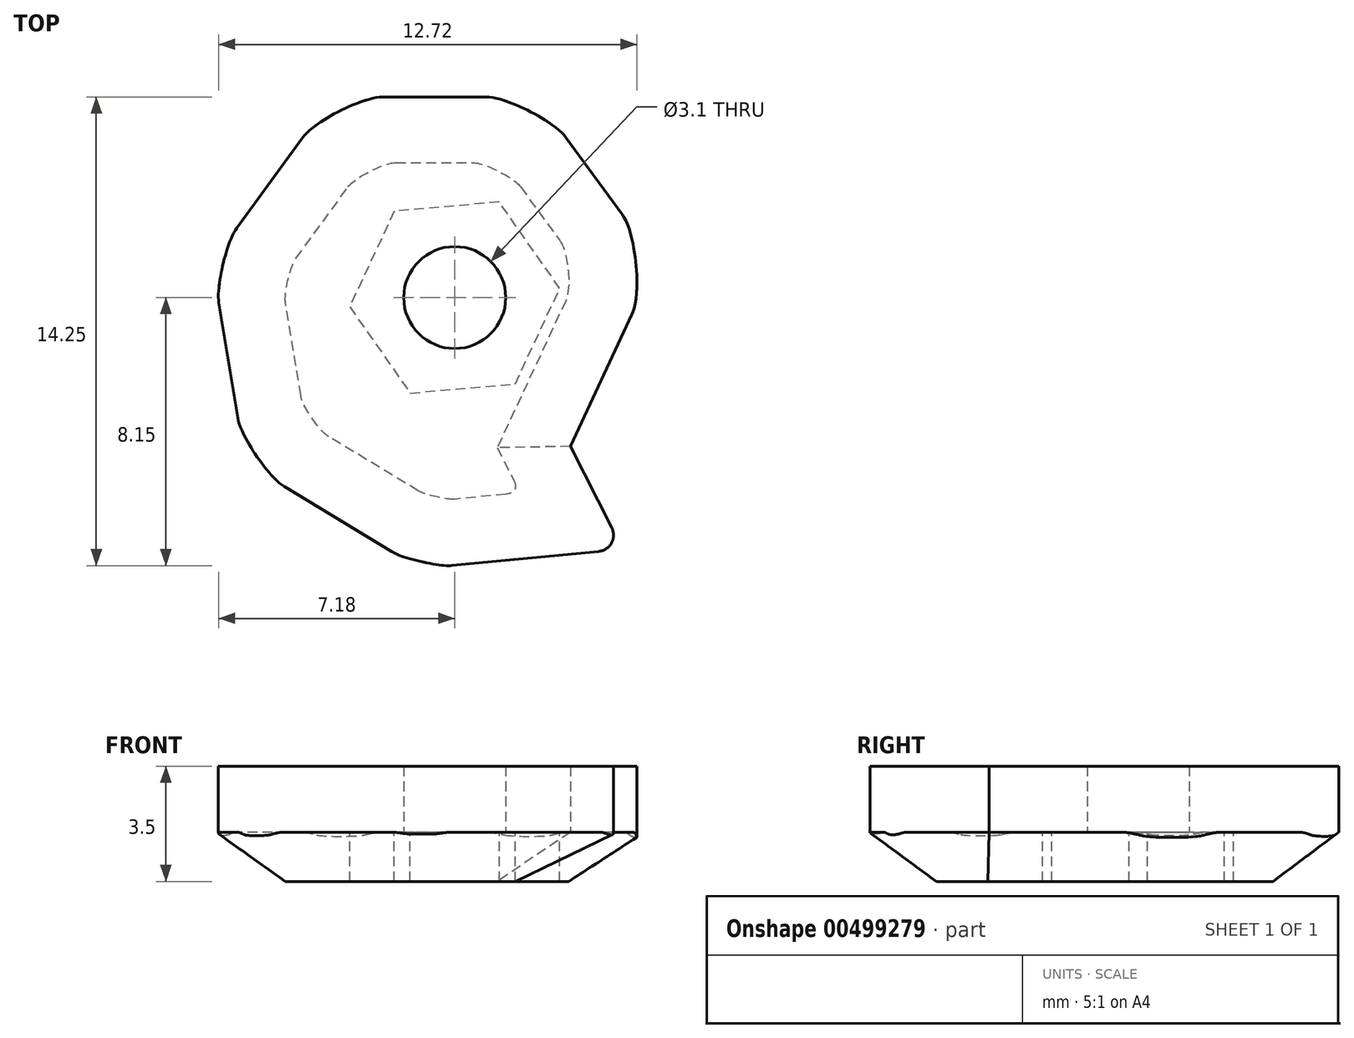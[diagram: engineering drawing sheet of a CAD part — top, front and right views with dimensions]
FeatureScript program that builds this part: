
annotation { "Feature Type Name" : "Feature", "Feature Type Description" : "" }
export const myFeature = defineFeature(function(context is Context, id is Id, definition is map)
    precondition{}
    {
        {
            var Q0;
            Q0=qCreatedBy(makeId("Top.planeOp"),FACE);
            var sketch = newSketch(context, id + "F0", { "sketchPlane" : qUnion([Q0])});
            skCircle(sketch, "E0", {"center": v(0, 0) * mm, "radius": 1.55 * mm});
            skLineSegment(sketch, "E1", {"start": v(0, 0) * mm, "end": v(4.62, -2.15) * mm, "construction": true});
            skLineSegment(sketch, "E2", {"start": v(0, 0) * mm, "end": v(4.52, 3.3) * mm, "construction": true});
            skLineSegment(sketch, "E3", {"start": v(0, 0) * mm, "end": v(0, 6.1) * mm, "construction": true});
            skLineSegment(sketch, "E4", {"start": v(0, 0) * mm, "end": v(-7, -1.15) * mm, "construction": true});
            skLineSegment(sketch, "E5", {"start": v(3.52, -4.53) * mm, "end": v(6.14, 1.1) * mm});
            skLineSegment(sketch, "E6", {"start": v(6.14, 1.1) * mm, "end": v(2.48, 6.1) * mm});
            skLineSegment(sketch, "E7", {"start": v(2.48, 6.1) * mm, "end": v(-3.72, 6.1) * mm});
            skLineSegment(sketch, "E8", {"start": v(-7.37, 1.1) * mm, "end": v(-6.37, -5.03) * mm});
            skLineSegment(sketch, "E9", {"start": v(0, 0) * mm, "end": v(-5.33, 3.9) * mm, "construction": true});
            skLineSegment(sketch, "E10", {"start": v(-3.72, 6.1) * mm, "end": v(-7.37, 1.1) * mm});
            skLineSegment(sketch, "E11", {"start": v(0, 0) * mm, "end": v(-3.94, -6.5) * mm, "construction": true});
            skLineSegment(sketch, "E12", {"start": v(-6.37, -5.03) * mm, "end": v(-1.07, -8.24) * mm});
            skLineSegment(sketch, "E13", {"start": v(0, 0) * mm, "end": v(0.77, -8.06) * mm, "construction": true});
            skLineSegment(sketch, "E14", {"start": v(-1.07, -8.24) * mm, "end": v(5.1, -7.65) * mm});
            skLineSegment(sketch, "E15", {"start": v(5.1, -7.65) * mm, "end": v(3.52, -4.53) * mm});
            skSolve(sketch);
        }
        {
            var Q0;
            Q0=makeQuery(id+"F0.imprint","IMPRINT",FACE,{"disambiguationData":[TD([[makeQuery(id+"F0.imprint","IMPRINT",EDGE,{"derivedFrom":sQuery(id+"F0.wireOp",EDGE,"E0")}),-1.0]])]});
            extrude(context, id + "F1", {"entities" : qUnion([Q0]), "depth" : 2 * mm});
        }
        {
            var Q0;
            Q0=makeQuery(id+"F1.opExtrude","CAP_FACE",FACE,{"disambiguationData":[OSD([sQuery(id+"F0.wireOp",EDGE,"E0"),sQuery(id+"F0.wireOp",EDGE,"E5"),sQuery(id+"F0.wireOp",EDGE,"E6"),sQuery(id+"F0.wireOp",EDGE,"E7"),sQuery(id+"F0.wireOp",EDGE,"E8"),sQuery(id+"F0.wireOp",EDGE,"E10"),sQuery(id+"F0.wireOp",EDGE,"E12"),sQuery(id+"F0.wireOp",EDGE,"E14"),sQuery(id+"F0.wireOp",EDGE,"E15")])],"isStart":true});
            var sketch = newSketch(context, id + "F2", { "sketchPlane" : qUnion([Q0])});
            skCircle(sketch, "E16.cCircle", {"center": v(0, 0) * mm, "radius": 2.77 * mm, "construction": true});
            skLineSegment(sketch, "E16.0", {"start": v(3.2, -0.28) * mm, "end": v(1.35, -2.9) * mm});
            skLineSegment(sketch, "E16.1", {"start": v(1.35, -2.9) * mm, "end": v(-1.84, -2.62) * mm});
            skLineSegment(sketch, "E16.2", {"start": v(-1.84, -2.62) * mm, "end": v(-3.2, 0.28) * mm});
            skLineSegment(sketch, "E16.3", {"start": v(-3.2, 0.28) * mm, "end": v(-1.35, 2.9) * mm});
            skLineSegment(sketch, "E16.4", {"start": v(-1.35, 2.9) * mm, "end": v(1.84, 2.62) * mm});
            skLineSegment(sketch, "E16.5", {"start": v(1.84, 2.62) * mm, "end": v(3.2, -0.28) * mm});
            skPoint(sketch, "E16.0.midPoint", {"position": v(2.27, -1.6) * mm});
            skSolve(sketch);
        }
        {
            var Q0;
            Q0=makeQuery(id+"F2.imprint","IMPRINT",FACE,{"disambiguationData":[TD([[makeQuery(id+"F2.imprint","IMPRINT",EDGE,{"derivedFrom":sQuery(id+"F2.wireOp",EDGE,"E16.0")}),1.0]])]});
            extrude(context, id + "F3", {"entities" : qUnion([Q0]), "operationType" : NewBodyOperationType.ADD, "depth" : 1.5 * mm});
        }
        {
            var Q0;
            Q0=makeQuery(id+"F3.opExtrude","CAP_EDGE",EDGE,{"disambiguationData":[OSD([sQuery(id+"F0.wireOp",EDGE,"E5")])],"isStart":false});
            var Q1;
            Q1=makeQuery(id+"F3.opExtrude","CAP_EDGE",EDGE,{"disambiguationData":[OSD([sQuery(id+"F0.wireOp",EDGE,"E15")])],"isStart":false});
            var Q2;
            Q2=makeQuery(id+"F3.opExtrude","CAP_EDGE",EDGE,{"disambiguationData":[OSD([sQuery(id+"F0.wireOp",EDGE,"E14")])],"isStart":false});
            var Q3;
            Q3=makeQuery(id+"F3.opExtrude","CAP_EDGE",EDGE,{"disambiguationData":[OSD([sQuery(id+"F0.wireOp",EDGE,"E12")])],"isStart":false});
            var Q4;
            Q4=makeQuery(id+"F3.opExtrude","CAP_EDGE",EDGE,{"disambiguationData":[OSD([sQuery(id+"F0.wireOp",EDGE,"E8")])],"isStart":false});
            var Q5;
            Q5=makeQuery(id+"F3.opExtrude","CAP_EDGE",EDGE,{"disambiguationData":[OSD([sQuery(id+"F0.wireOp",EDGE,"E10")])],"isStart":false});
            var Q6;
            Q6=makeQuery(id+"F3.opExtrude","CAP_EDGE",EDGE,{"disambiguationData":[OSD([sQuery(id+"F0.wireOp",EDGE,"E7")])],"isStart":false});
            var Q7;
            Q7=makeQuery(id+"F3.opExtrude","CAP_EDGE",EDGE,{"disambiguationData":[OSD([sQuery(id+"F0.wireOp",EDGE,"E6")])],"isStart":false});
            chamfer(context, id + "F4", {"entities" : qUnion([Q0, Q1, Q2, Q3, Q4, Q5, Q6, Q7]), "chamferType" : ChamferType.TWO_OFFSETS, "width1" : 1.5 * mm, "oppositeDirection" : false, "width2" : 2 * mm, "tangentPropagation" : true});
        }
        {
            var Q0;
            {var subQ0=sQuery(id+"F0.wireOp",EDGE,"E12");var subQ1=sQuery(id+"F0.wireOp",EDGE,"E8");Q0=makeQuery(id+"F3.boolean.opBoolean","MERGE",EDGE,{"derivedFrom":[makeQuery(id+"F1.opExtrude","SWEPT_EDGE",EDGE,{"disambiguationData":[OSD([subQ1,subQ0])]}),makeQuery(id+"F3.opExtrude","SWEPT_EDGE",EDGE,{"disambiguationData":[OSD([subQ1,subQ0])]})]});}
            var Q1;
            Q1=makeQuery(id+"F4.opChamfer","BLEND_EDGE",EDGE,{"blendedFrom":[makeQuery(id+"F3.opExtrude","CAP_EDGE",EDGE,{"disambiguationData":[OSD([sQuery(id+"F0.wireOp",EDGE,"E8")])],"isStart":false}),makeQuery(id+"F3.opExtrude","CAP_EDGE",EDGE,{"disambiguationData":[OSD([sQuery(id+"F0.wireOp",EDGE,"E12")])],"isStart":false})],"blendedInto":[]});
            var Q2;
            {var subQ0=sQuery(id+"F0.wireOp",EDGE,"E10");var subQ1=sQuery(id+"F0.wireOp",EDGE,"E8");Q2=makeQuery(id+"F3.boolean.opBoolean","MERGE",EDGE,{"derivedFrom":[makeQuery(id+"F1.opExtrude","SWEPT_EDGE",EDGE,{"disambiguationData":[OSD([subQ1,subQ0])]}),makeQuery(id+"F3.opExtrude","SWEPT_EDGE",EDGE,{"disambiguationData":[OSD([subQ1,subQ0])]})]});}
            var Q3;
            Q3=makeQuery(id+"F4.opChamfer","BLEND_EDGE",EDGE,{"blendedFrom":[makeQuery(id+"F3.opExtrude","CAP_EDGE",EDGE,{"disambiguationData":[OSD([sQuery(id+"F0.wireOp",EDGE,"E8")])],"isStart":false}),makeQuery(id+"F3.opExtrude","CAP_EDGE",EDGE,{"disambiguationData":[OSD([sQuery(id+"F0.wireOp",EDGE,"E10")])],"isStart":false})],"blendedInto":[]});
            var Q4;
            Q4=makeQuery(id+"F4.opChamfer","BLEND_EDGE",EDGE,{"blendedFrom":[makeQuery(id+"F3.opExtrude","CAP_EDGE",EDGE,{"disambiguationData":[OSD([sQuery(id+"F0.wireOp",EDGE,"E7")])],"isStart":false}),makeQuery(id+"F3.opExtrude","CAP_EDGE",EDGE,{"disambiguationData":[OSD([sQuery(id+"F0.wireOp",EDGE,"E10")])],"isStart":false})],"blendedInto":[]});
            var Q5;
            {var subQ0=sQuery(id+"F0.wireOp",EDGE,"E10");var subQ1=sQuery(id+"F0.wireOp",EDGE,"E7");Q5=makeQuery(id+"F3.boolean.opBoolean","MERGE",EDGE,{"derivedFrom":[makeQuery(id+"F1.opExtrude","SWEPT_EDGE",EDGE,{"disambiguationData":[OSD([subQ1,subQ0])]}),makeQuery(id+"F3.opExtrude","SWEPT_EDGE",EDGE,{"disambiguationData":[OSD([subQ1,subQ0])]})]});}
            var Q6;
            Q6=makeQuery(id+"F4.opChamfer","BLEND_EDGE",EDGE,{"blendedFrom":[makeQuery(id+"F3.opExtrude","CAP_EDGE",EDGE,{"disambiguationData":[OSD([sQuery(id+"F0.wireOp",EDGE,"E6")])],"isStart":false}),makeQuery(id+"F3.opExtrude","CAP_EDGE",EDGE,{"disambiguationData":[OSD([sQuery(id+"F0.wireOp",EDGE,"E7")])],"isStart":false})],"blendedInto":[]});
            var Q7;
            {var subQ0=sQuery(id+"F0.wireOp",EDGE,"E7");var subQ1=sQuery(id+"F0.wireOp",EDGE,"E6");Q7=makeQuery(id+"F3.boolean.opBoolean","MERGE",EDGE,{"derivedFrom":[makeQuery(id+"F1.opExtrude","SWEPT_EDGE",EDGE,{"disambiguationData":[OSD([subQ1,subQ0])]}),makeQuery(id+"F3.opExtrude","SWEPT_EDGE",EDGE,{"disambiguationData":[OSD([subQ1,subQ0])]})]});}
            var Q8;
            Q8=makeQuery(id+"F4.opChamfer","BLEND_EDGE",EDGE,{"blendedFrom":[makeQuery(id+"F3.opExtrude","CAP_EDGE",EDGE,{"disambiguationData":[OSD([sQuery(id+"F0.wireOp",EDGE,"E5")])],"isStart":false}),makeQuery(id+"F3.opExtrude","CAP_EDGE",EDGE,{"disambiguationData":[OSD([sQuery(id+"F0.wireOp",EDGE,"E6")])],"isStart":false})],"blendedInto":[]});
            var Q9;
            {var subQ0=sQuery(id+"F0.wireOp",EDGE,"E6");var subQ1=sQuery(id+"F0.wireOp",EDGE,"E5");Q9=makeQuery(id+"F3.boolean.opBoolean","MERGE",EDGE,{"derivedFrom":[makeQuery(id+"F1.opExtrude","SWEPT_EDGE",EDGE,{"disambiguationData":[OSD([subQ1,subQ0])]}),makeQuery(id+"F3.opExtrude","SWEPT_EDGE",EDGE,{"disambiguationData":[OSD([subQ1,subQ0])]})]});}
            var Q10;
            {var subQ0=sQuery(id+"F0.wireOp",EDGE,"E14");var subQ1=sQuery(id+"F0.wireOp",EDGE,"E12");Q10=makeQuery(id+"F3.boolean.opBoolean","MERGE",EDGE,{"derivedFrom":[makeQuery(id+"F1.opExtrude","SWEPT_EDGE",EDGE,{"disambiguationData":[OSD([subQ1,subQ0])]}),makeQuery(id+"F3.opExtrude","SWEPT_EDGE",EDGE,{"disambiguationData":[OSD([subQ1,subQ0])]})]});}
            var Q11;
            Q11=makeQuery(id+"F4.opChamfer","BLEND_EDGE",EDGE,{"blendedFrom":[makeQuery(id+"F3.opExtrude","CAP_EDGE",EDGE,{"disambiguationData":[OSD([sQuery(id+"F0.wireOp",EDGE,"E12")])],"isStart":false}),makeQuery(id+"F3.opExtrude","CAP_EDGE",EDGE,{"disambiguationData":[OSD([sQuery(id+"F0.wireOp",EDGE,"E14")])],"isStart":false})],"blendedInto":[]});
            fillet(context, id + "F5", {"entities" : qUnion([Q0, Q1, Q2, Q3, Q4, Q5, Q6, Q7, Q8, Q9, Q10, Q11]), "radius" : 3 * mm, "tangentPropagation" : true, "rho" : 0.3, "crossSection" : FilletCrossSection.CONIC, "allowEdgeOverflow" : false});
        }
        {
            var Q0;
            {var subQ0=sQuery(id+"F0.wireOp",EDGE,"E15");var subQ1=sQuery(id+"F0.wireOp",EDGE,"E14");Q0=makeQuery(id+"F3.boolean.opBoolean","MERGE",EDGE,{"derivedFrom":[makeQuery(id+"F1.opExtrude","SWEPT_EDGE",EDGE,{"disambiguationData":[OSD([subQ1,subQ0])]}),makeQuery(id+"F3.opExtrude","SWEPT_EDGE",EDGE,{"disambiguationData":[OSD([subQ1,subQ0])]})]});}
            var Q1;
            Q1=makeQuery(id+"F4.opChamfer","BLEND_EDGE",EDGE,{"blendedFrom":[makeQuery(id+"F3.opExtrude","CAP_EDGE",EDGE,{"disambiguationData":[OSD([sQuery(id+"F0.wireOp",EDGE,"E14")])],"isStart":false}),makeQuery(id+"F3.opExtrude","CAP_EDGE",EDGE,{"disambiguationData":[OSD([sQuery(id+"F0.wireOp",EDGE,"E15")])],"isStart":false})],"blendedInto":[]});
            fillet(context, id + "F6", {"entities" : qUnion([Q0, Q1]), "radius" : 0.5 * mm, "tangentPropagation" : true, "allowEdgeOverflow" : false});
        }
    });
